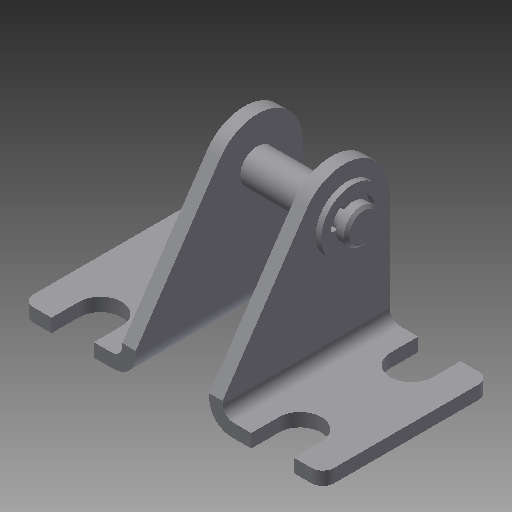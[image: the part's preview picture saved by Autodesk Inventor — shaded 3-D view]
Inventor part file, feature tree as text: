
AUTODESK INVENTOR PART (.ipt)
format: ipt  version: 2018 (Build 220112000, 112)  size: 281,088 bytes
history: native  units: in
note: dims shown in document units (in); Inventor stores cm internally (conversion verified against a paired STEP export)
features: imported_body x5, fillet x2, other x2, revolve x1, mirror x1
ambient origin geometry x8: Origin, YZ Plane, XZ Plane, XY Plane, X Axis, Y Axis, Z Axis, Center Point
bodies: Body1 (feature_tree), Body2 (feature_tree), Body3 (feature_tree), Body4 (feature_tree), Body5 (feature_tree)
feature tree (11):
  fillet  "Fillet2"  [1 undecoded]
  other  "Cylinder_9-16bore_bracket1"
  fillet  "Fillet4"  [1 undecoded]
  revolve  "Revolve1"  [1 undecoded]
  other  "Boss-Extrude5"
  mirror  "Mirror1"
  imported_body  "Base1"
  imported_body  "Base2"
  imported_body  "Base3"
  imported_body  "Base4"
  imported_body  "Base5"
note: 3 required parameter values undecoded (feature->parameter linkage not recoverable at this tier; creation-order binding heuristic only, values carry confidence <= 0.55)
